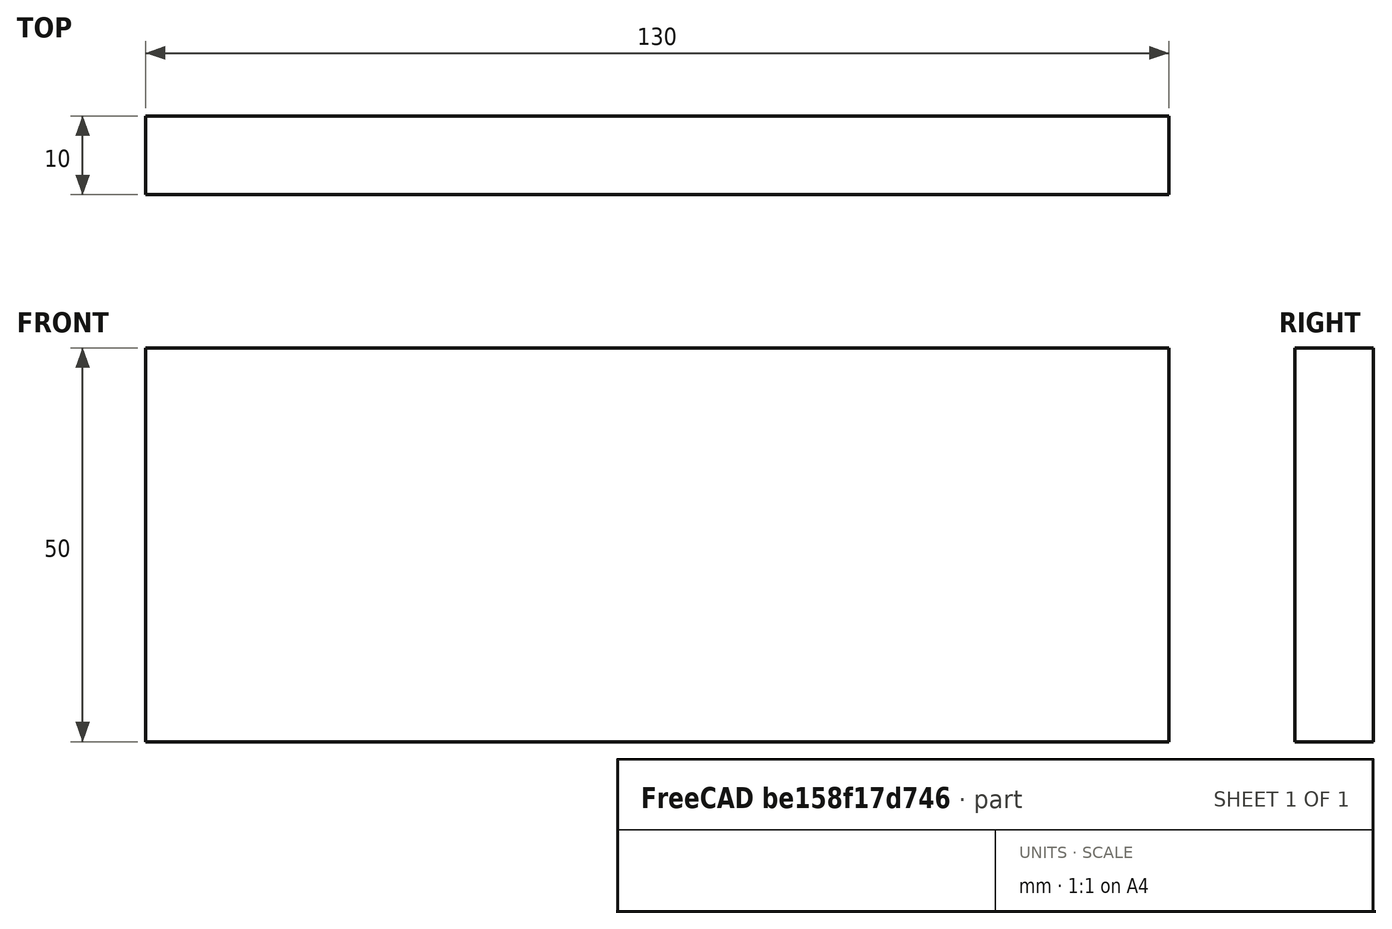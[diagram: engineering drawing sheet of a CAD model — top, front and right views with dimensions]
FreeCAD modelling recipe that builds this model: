
FCSTD DOCUMENT  (FreeCAD 0.15R4671 (Git))
Label: Flat Bar 130x10 EN10058 S235JR
License: All rights reserved
LicenseURL: http://en.wikipedia.org/wiki/All_rights_reserved
objects: Sketcher::SketchObject×1, Part::Extrusion×1
note: 2 computed .brp shape members not serialized (recipe doc carries the construction recipe); baked Part::Feature solids carry a one-line shape summary decoded from their .brp

FEATURE [Sketcher::SketchObject] Sketch
  sketch-geometry (4):
    g0: LineSegment StartX=-65 StartY=-5 StartZ=0 EndX=65 EndY=-5 EndZ=0
    g1: LineSegment StartX=65 StartY=-5 StartZ=0 EndX=65 EndY=5 EndZ=0
    g2: LineSegment StartX=65 StartY=5 StartZ=0 EndX=-65 EndY=5 EndZ=0
    g3: LineSegment StartX=-65 StartY=5 StartZ=0 EndX=-65 EndY=-5 EndZ=0
  constraints (12):
    c: Coincident(g0,g1)
    c: Coincident(g1,g2)
    c: Coincident(g2,g3)
    c: Coincident(g3,g0)
    c: Horizontal(g0)
    c: Horizontal(g2)
    c: Vertical(g1)
    c: Vertical(g3)
    c: Symmetric(g1,g2,g-2)
    c: Symmetric(g0,g1,g-1)
    c: DistanceY(g1) = 10
    c: DistanceX(g0) = 130
FEATURE [Part::Extrusion] Extrude  label="Flat Bar 130x10 EN10058 S235JR"
  Base = -> Sketch
  Dir = (0,0,50)
  Solid = true
